# Revit family: 3910
name_source: partatom
category: Arredi
revit_build: Autodesk Revit 2016 (Build: 20151007_0715(x64)
units: mm (PartAtom-declared; Revit-internal decimal feet)

## family parameters
Basato su piano di lavoro = No
Condiviso = No
Numero OmniClass = 23.40.20.00
Punto di calcolo locali = No
Sempre verticale = Sì
Taglio con vuoti quando caricato = No
Titolo OmniClass = General Furniture and Specialties

## types (1)
- 3910
    Arper - Legs material = Arper - Generic wood
    Descrizione = Chair with reconstituted veneer four-leg base and shell, with natural
birchwood effect or stained in four different colours.  Shell and base
can be ordered with the same finish or different finishes can be
combined together. Optional glides with felt for wooden floors are
available upon request. A non-washable, removable cover (Item
3920) is also  available in leather, faux leather, fabric or customer's
material allowing the chair to be used in two versions:  wood or
upholstered.
    Modello = Aava
    Produttore = ARPER s.p.a.
    URL = http://www.arper.com
